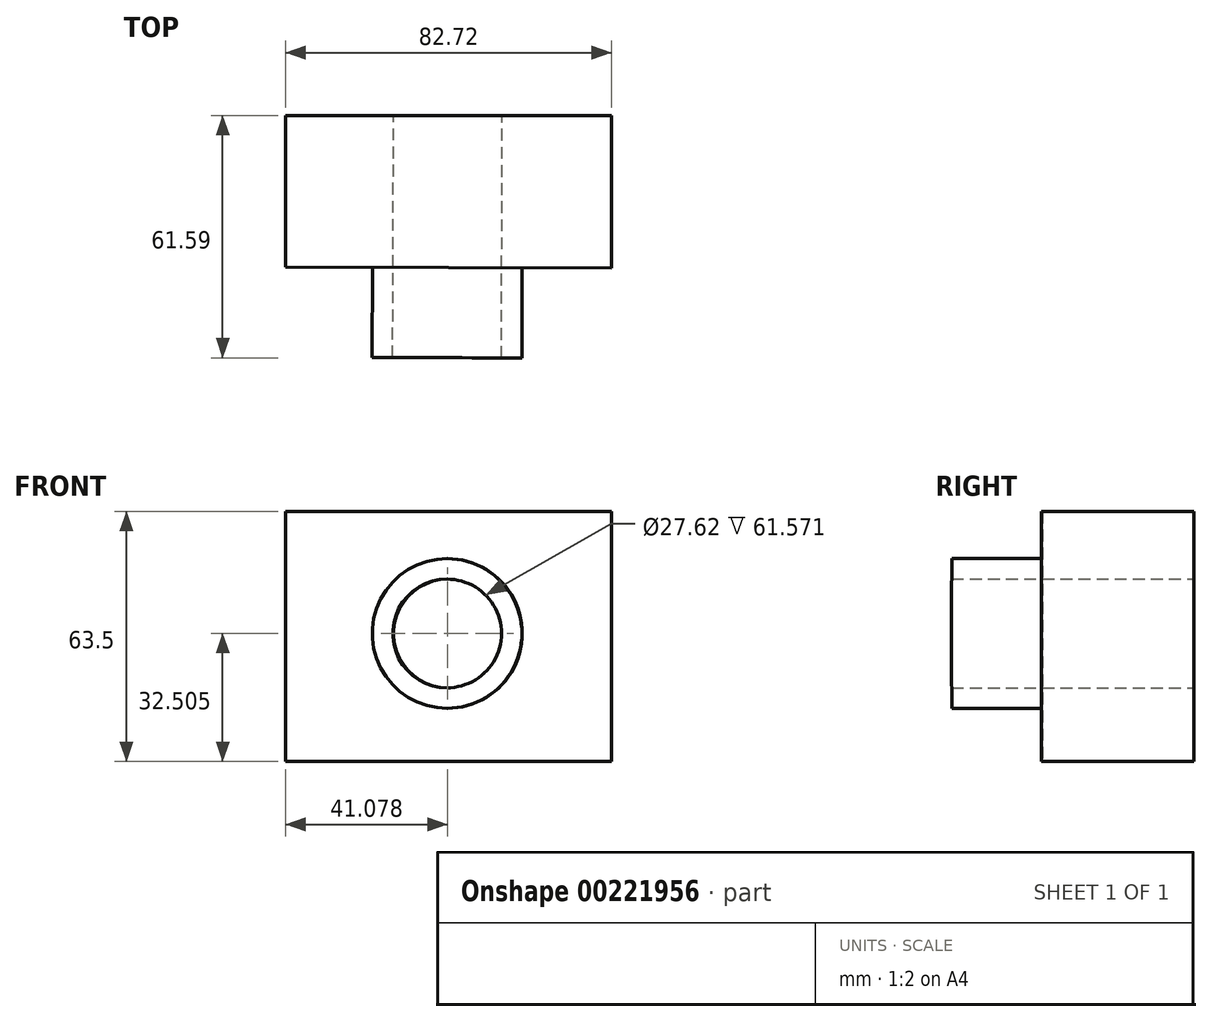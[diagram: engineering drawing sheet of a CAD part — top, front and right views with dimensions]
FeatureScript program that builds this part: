
annotation { "Feature Type Name" : "Feature", "Feature Type Description" : "" }
export const myFeature = defineFeature(function(context is Context, id is Id, definition is map)
    precondition{}
    {
        {
            var Q0;
            Q0=qCreatedBy(makeId("Top.planeOp"),FACE);
            var sketch = newSketch(context, id + "F0", { "sketchPlane" : qUnion([Q0])});
            skLineSegment(sketch, "E0", {"start": v(56.5, -76.03) * mm, "end": v(56.5, -37.22) * mm});
            skLineSegment(sketch, "E1", {"start": v(56.5, -37.22) * mm, "end": v(-26.21, -37.22) * mm});
            skLineSegment(sketch, "E2", {"start": v(-26.21, -37.22) * mm, "end": v(-26.21, -75.75) * mm});
            skLineSegment(sketch, "E3", {"start": v(-26.21, -75.75) * mm, "end": v(56.5, -76.03) * mm});
            skSolve(sketch);
        }
        {
            var Q0;
            Q0 = qSketchRegion(id + "F0", true);
            extrude(context, id + "F1", {"entities" : qUnion([Q0]), "depth" : 63.5 * mm});
        }
        {
            var Q0;
            Q0=makeQuery(id+"F1.opExtrude","SWEPT_FACE",FACE,{"disambiguationData":[OSD([sQuery(id+"F0.wireOp",EDGE,"E3")])]});
            var sketch = newSketch(context, id + "F2", { "sketchPlane" : qUnion([Q0])});
            skCircle(sketch, "E4", {"center": v(15.1, 32.5) * mm, "radius": 19.03 * mm});
            skSolve(sketch);
        }
        {
            var Q0;
            Q0 = qSketchRegion(id + "F2", true);
            extrude(context, id + "F3", {"entities" : qUnion([Q0]), "operationType" : NewBodyOperationType.ADD, "depth" : 22.86 * mm});
        }
        {
            var Q0;
            Q0=makeQuery(id+"F3.opExtrude","CAP_FACE",FACE,{"disambiguationData":[OSD([sQuery(id+"F2.wireOp",EDGE,"E4")])],"isStart":false});
            var sketch = newSketch(context, id + "F4", { "sketchPlane" : qUnion([Q0])});
            skCircle(sketch, "E5", {"center": v(15.1, 32.5) * mm, "radius": 13.81 * mm});
            skSolve(sketch);
        }
        {
            var Q0;
            Q0 = qSketchRegion(id + "F4", true);
            extrude(context, id + "F5", {"entities" : qUnion([Q0]), "operationType" : NewBodyOperationType.REMOVE, "endBound" : BoundingType.THROUGH_ALL, "depth" : 25.4 * mm, "hasSecondDirection" : true, "secondDirectionBound" : SecondDirectionBoundingType.THROUGH_ALL, "secondDirectionOppositeDirection" : true, "secondDirectionDepth" : 25.4 * mm});
        }
    });
